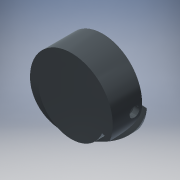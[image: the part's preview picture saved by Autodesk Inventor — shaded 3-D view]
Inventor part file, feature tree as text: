
AUTODESK INVENTOR PART (.ipt)
format: ipt  version: 2016 (Build 200138000, 138)  size: 359,936 bytes
history: native  units: mm
features: sketch x9, other x5, extrude x5, plane x2, fillet x2, hole x2, projected_geometry x2, surface_op x1, loft x1
ambient origin geometry x8: Origin, YZ Plane, XZ Plane, XY Plane, X Axis, Y Axis, Z Axis, Center Point
bodies: Solid1 (feature_tree)
feature tree (29):
  other  "Fixture.ipt"
  extrude  "Extrusion1"  TaperAngle=0.0deg  [1 undecoded]
  plane  "Work Plane4"
  sketch  "Sketch4"  dims[d2=21.0mm d3=0.0mm]
  sketch  "3D Sketch5"
  sketch  "3D Sketch6"
  surface_op  "Sculpt3"
  extrude  "Extrusion2"  Depth=21.0mm
  extrude  "Extrusion3"  Depth=1.9mm TaperAngle=0.0deg
  extrude  "Extrusion4"  TaperAngle=0.0deg  [1 undecoded]
  fillet  "Fillet5"  Radius=4.65mm
  plane  "Work Plane5"
  sketch  "Sketch15"  dims[d74=10.0mm d75=50.9mm d76=5.0mm d77=159.907066mm d79=1.047198mm d81=1.047198mm d82=10.0mm d83=21.0mm d84=0.0mm d85=90.0deg d86=0.0mm d87=90.0deg d88=17.9mm d89=0.1mm d90=3.1mm d91=6.0mm d92=4.0mm d93=2.0mm d94=90.0deg d95=8.0mm d96=20.594885mm d97=6.0mm d98=6.0mm d99=4.0mm d100=2.0mm d101=90.0deg d102=3.449977mm d103=20.594885mm]
  hole  "Hole5"  [1 undecoded]
  sketch  "3D Sketch7"
  hole  "Hole6"  [1 undecoded]
  fillet  "Fillet2"  Radius=5.0mm
  other  "Srf1"
  sketch  "Sketch5"  dims[d15=5.3mm d16=21.0mm]
  sketch  "Sketch7"  dims[d17=0.0mm d24=1.9mm d25=0.0mm]
  sketch  "Sketch9"  dims[d40=6.1mm d41=0.0mm d57=4.65mm]
  sketch  "Sketch12"  dims[d58=14.55mm d59=0.0mm d60=3.0mm]
  projected_geometry  "Projected Loop3"
  other  "Project to Surface6"
  other  "Project to Surface7"
  other  "Srf4"
  projected_geometry  "Projected Loop4"
  extrude  "ExtrusionSrf1"  Depth=10.0mm
  loft  "LoftSrf3"
note: 4 required parameter values undecoded (feature->parameter linkage not recoverable at this tier; creation-order binding heuristic only, values carry confidence <= 0.55)
